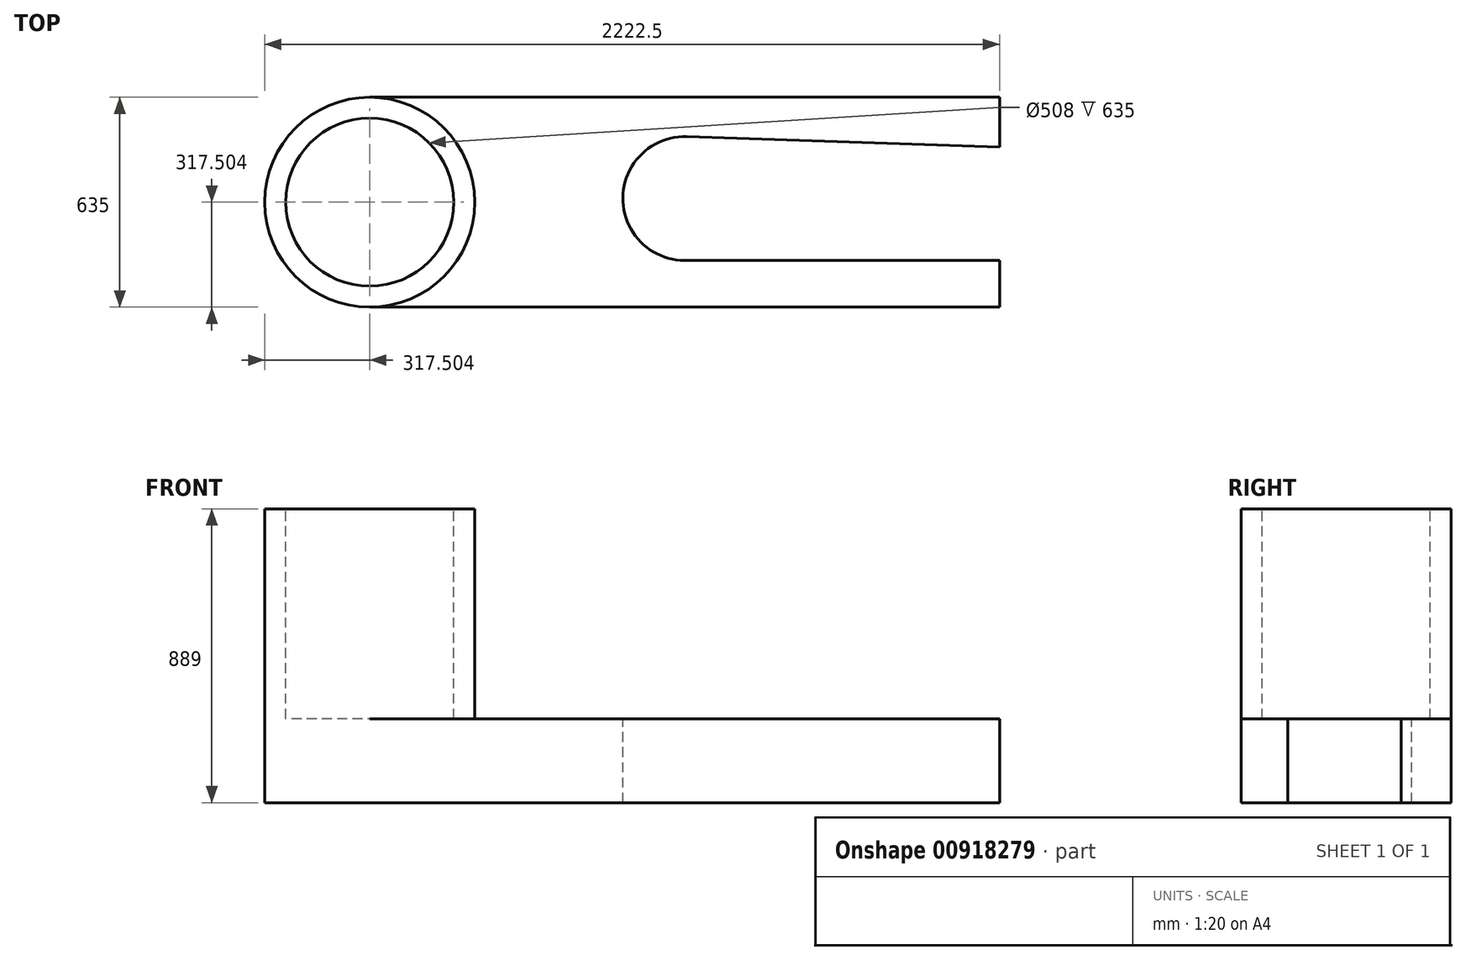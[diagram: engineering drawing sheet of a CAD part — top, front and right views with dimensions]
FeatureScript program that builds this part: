
annotation { "Feature Type Name" : "Feature", "Feature Type Description" : "" }
export const myFeature = defineFeature(function(context is Context, id is Id, definition is map)
    precondition{}
    {
        {
            var Q0;
            Q0=qCreatedBy(makeId("Top.planeOp"),FACE);
            var sketch = newSketch(context, id + "F0", { "sketchPlane" : qUnion([Q0])});
            skLineSegment(sketch, "E0.bottom", {"start": v(-774.84, 432.2) * mm, "end": v(1130.16, 432.2) * mm});
            skLineSegment(sketch, "E0.top", {"start": v(-774.84, -202.8) * mm, "end": v(1130.16, -202.8) * mm});
            skLineSegment(sketch, "E0.left", {"start": v(-774.84, 432.2) * mm, "end": v(-774.84, -202.8) * mm});
            skLineSegment(sketch, "E0.right", {"start": v(1130.16, 432.2) * mm, "end": v(1130.16, -202.8) * mm});
            skSolve(sketch);
        }
        {
            var Q0;
            Q0 = qSketchRegion(id + "F0", true);
            extrude(context, id + "F1", {"entities" : qUnion([Q0]), "endBound" : BoundingType.SYMMETRIC, "depth" : 254 * mm, "offsetDistance" : 25.4 * mm});
        }
        {
            var Q0;
            Q0=makeQuery(id+"F1.opExtrude","CAP_FACE",FACE,{"disambiguationData":[OSD([sQuery(id+"F0.wireOp",EDGE,"E0.bottom"),sQuery(id+"F0.wireOp",EDGE,"E0.top"),sQuery(id+"F0.wireOp",EDGE,"E0.left"),sQuery(id+"F0.wireOp",EDGE,"E0.right")])],"isStart":false});
            var sketch = newSketch(context, id + "F2", { "sketchPlane" : qUnion([Q0])});
            skCircle(sketch, "E1", {"center": v(-774.84, 114.7) * mm, "radius": 317.5 * mm});
            skSolve(sketch);
        }
        {
            var Q0;
            Q0 = qSketchRegion(id + "F2", true);
            extrude(context, id + "F3", {"entities" : qUnion([Q0]), "operationType" : NewBodyOperationType.ADD, "endBound" : BoundingType.SYMMETRIC, "depth" : 254 * mm, "offsetDistance" : 25.4 * mm});
        }
        {
            var Q0;
            Q0=makeQuery(id+"F3.opExtrude","CAP_FACE",FACE,{"disambiguationData":[OSD([sQuery(id+"F2.wireOp",EDGE,"E1")])],"isStart":true});
            extrude(context, id + "F4", {"entities" : qUnion([Q0]), "operationType" : NewBodyOperationType.ADD, "depth" : 127 * mm, "offsetDistance" : 25.4 * mm});
        }
        {
            var Q0;
            Q0=makeQuery(id+"F3.opExtrude","CAP_FACE",FACE,{"disambiguationData":[OSD([sQuery(id+"F2.wireOp",EDGE,"E1")])],"isStart":false});
            extrude(context, id + "F5", {"entities" : qUnion([Q0]), "operationType" : NewBodyOperationType.ADD, "depth" : 508 * mm, "offsetDistance" : 25.4 * mm});
        }
        {
            var Q0;
            Q0=makeQuery(id+"F5.opExtrude","CAP_FACE",FACE,{"disambiguationData":[OSD([sQuery(id+"F2.wireOp",EDGE,"E1")])],"isStart":false});
            var sketch = newSketch(context, id + "F6", { "sketchPlane" : qUnion([Q0])});
            skCircle(sketch, "E2", {"center": v(-774.84, 114.7) * mm, "radius": 254 * mm});
            skSolve(sketch);
        }
        {
            var Q0;
            Q0=makeQuery(id+"F6.imprint","IMPRINT",FACE,{"disambiguationData":[TD([[makeQuery(id+"F6.imprint","IMPRINT",EDGE,{"derivedFrom":sQuery(id+"F6.wireOp",EDGE,"E2")}),1.0]])]});
            extrude(context, id + "F7", {"entities" : qUnion([Q0]), "operationType" : NewBodyOperationType.REMOVE, "oppositeDirection" : true, "depth" : 635 * mm, "offsetDistance" : 25.4 * mm});
        }
        {
            var Q0;
            Q0=makeQuery(id+"F1.opExtrude","CAP_FACE",FACE,{"disambiguationData":[OSD([sQuery(id+"F0.wireOp",EDGE,"E0.bottom"),sQuery(id+"F0.wireOp",EDGE,"E0.top"),sQuery(id+"F0.wireOp",EDGE,"E0.left"),sQuery(id+"F0.wireOp",EDGE,"E0.right")])],"isStart":false});
            var sketch = newSketch(context, id + "F8", { "sketchPlane" : qUnion([Q0])});
            skArc(sketch, "E3", {"start": v(183.87, 312.78) * mm, "mid": v(-9.34, 128.96) * mm, "end": v(177.66, -61.18) * mm});
            skPoint(sketch, "E3.centerSnap0", {"position": v(177.66, -202.8) * mm});
            skLineSegment(sketch, "E4", {"start": v(177.66, -61.18) * mm, "end": v(1130.16, -61.18) * mm});
            skLineSegment(sketch, "E5", {"start": v(183.87, 312.78) * mm, "end": v(1130.16, 281.34) * mm});
            skSolve(sketch);
        }
        {
            var Q0;
            Q0=makeQuery(id+"F8.imprint","IMPRINT",FACE,{"disambiguationData":[TD([[makeQuery(id+"F8.imprint","IMPRINT",EDGE,{"derivedFrom":sQuery(id+"F8.wireOp",EDGE,"E3")}),1.0]])]});
            extrude(context, id + "F9", {"entities" : qUnion([Q0]), "operationType" : NewBodyOperationType.REMOVE, "endBound" : BoundingType.THROUGH_ALL, "oppositeDirection" : true, "depth" : 25.4 * mm, "offsetDistance" : 25.4 * mm});
        }
    });
